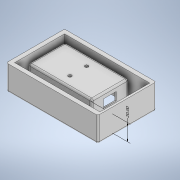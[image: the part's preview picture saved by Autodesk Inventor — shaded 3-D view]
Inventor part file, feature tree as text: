
AUTODESK INVENTOR PART (.ipt)
format: ipt  version: 2020 (Build 240168000, 168)  size: 230,912 bytes
history: native  units: mm
features: extrude x7, sketch x6, projected_geometry x4, fillet x3, other x2, hole x1
ambient origin geometry x8: Origin, YZ Plane, XZ Plane, XY Plane, X Axis, Y Axis, Z Axis, Center Point
bodies: Solid1 (feature_tree)
feature tree (23):
  other  "Annotations"
  sketch  "Sketch1"  dims[d0=100.0mm d1=60.0mm]
  extrude  "Extrusion1"  Depth=60.0mm
  extrude  "Extrusion2"  TaperAngle=180.0deg  [1 undecoded]
  extrude  "Extrusion3"  Depth=73.0mm
  extrude  "Extrusion4"  Depth=110.0mm
  extrude  "Extrusion5"  Depth=76.0mm
  fillet  "Fillet1"  Radius=44.0mm
  hole  "Hole1"  [1 undecoded]
  extrude  "Extrusion6"  Depth=2.5mm TaperAngle=0.0deg
  fillet  "Fillet2"  Radius=2.5mm
  extrude  "Extrusion7"  Depth=15.0mm
  fillet  "Fillet3"  Radius=10.0mm
  sketch  "Sketch2"  dims[d2=5.0mm d3=180.0deg]
  sketch  "Sketch4"  dims[d4=5.0mm d5=73.0mm]
  projected_geometry  "Projected Loop3"
  projected_geometry  "Projected Loop4"
  projected_geometry  "Projected Loop5"
  sketch  "Sketch5"  dims[d6=40.0mm d7=110.0mm]
  sketch  "Sketch6"  dims[d8=70.0mm d9=76.0mm d10=44.0mm]
  sketch  "Sketch7"  dims[d11=30.0mm d12=0.0mm d13=22.0mm d14=0.0mm d15=2.5mm d16=0.0mm d17=2.5mm d18=0.0mm d19=15.0mm d20=10.0mm d21=10.0mm d22=0.0mm d23=2.0mm d24=10.0mm d25=10.0mm d26=1.5mm d27=6.0mm d28=2.5mm d29=1.0mm d30=14.3117mm d31=40.0mm d32=20.594885mm d33=4.0mm d34=4.0mm d35=1.5mm d36=0.0mm d37=2.0mm d46=2.5mm d47=27.5mm d48=0.0mm d55=2.0mm d52=7.759428mm d53=7.333746mm d54=20.0mm]
  projected_geometry  "Project Cut Edges5"
  other  "Linear Dimension 2"
note: 2 required parameter values undecoded (feature->parameter linkage not recoverable at this tier; creation-order binding heuristic only, values carry confidence <= 0.55)
